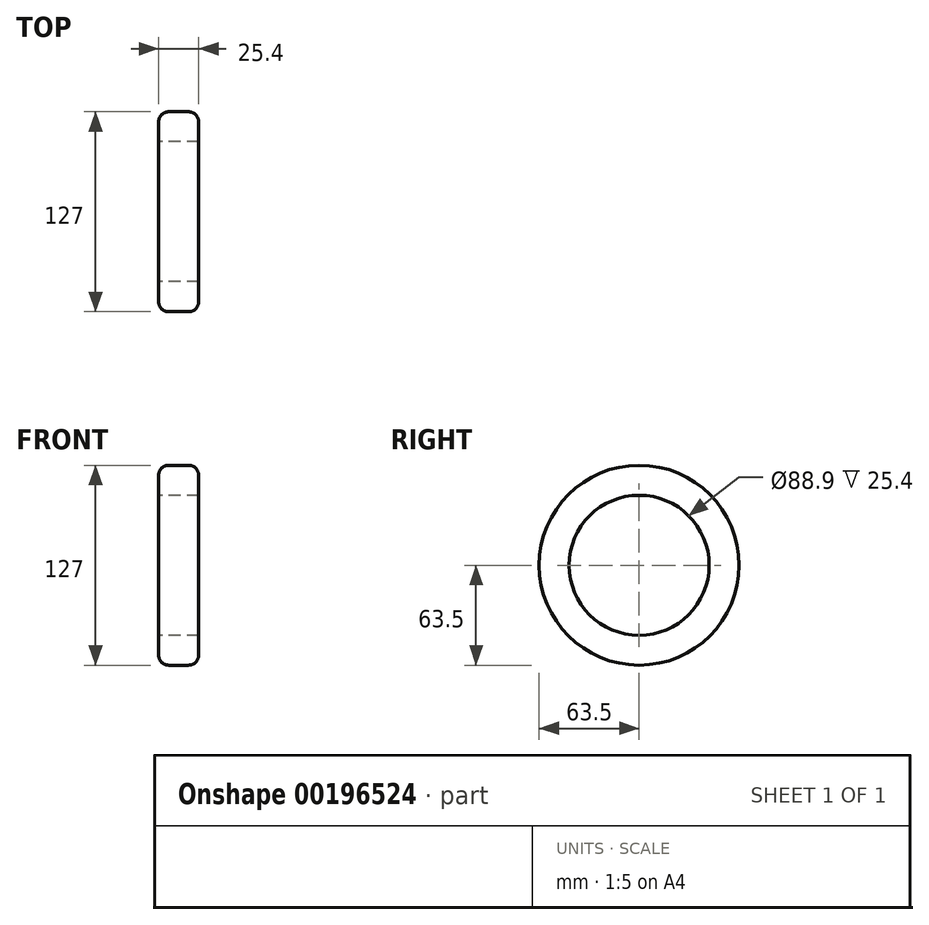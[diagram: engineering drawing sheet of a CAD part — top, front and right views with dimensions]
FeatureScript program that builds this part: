
annotation { "Feature Type Name" : "Feature", "Feature Type Description" : "" }
export const myFeature = defineFeature(function(context is Context, id is Id, definition is map)
    precondition{}
    {
        {
            var Q0;
            Q0=qCreatedBy(makeId("Right.planeOp"),FACE);
            var sketch = newSketch(context, id + "F0", { "sketchPlane" : qUnion([Q0])});
            skCircle(sketch, "E0", {"center": v(0, 0) * mm, "radius": 63.5 * mm});
            skCircle(sketch, "E1", {"center": v(0, 0) * mm, "radius": 44.45 * mm});
            skSolve(sketch);
        }
        {
            var Q0;
            Q0 = qSketchRegion(id + "F0", true);
            extrude(context, id + "F1", {"entities" : qUnion([Q0]), "depth" : 25.4 * mm});
        }
        {
            var Q0;
            Q0=makeQuery(id+"F1.opExtrude","CAP_EDGE",EDGE,{"disambiguationData":[OSD([sQuery(id+"F0.wireOp",EDGE,"E0")])],"isStart":false});
            var Q1;
            Q1=makeQuery(id+"F1.opExtrude","CAP_EDGE",EDGE,{"disambiguationData":[OSD([sQuery(id+"F0.wireOp",EDGE,"E0")])],"isStart":true});
            fillet(context, id + "F2", {"entities" : qUnion([Q0, Q1]), "radius" : 6.35 * mm, "tangentPropagation" : true, "allowEdgeOverflow" : false});
        }
    });
